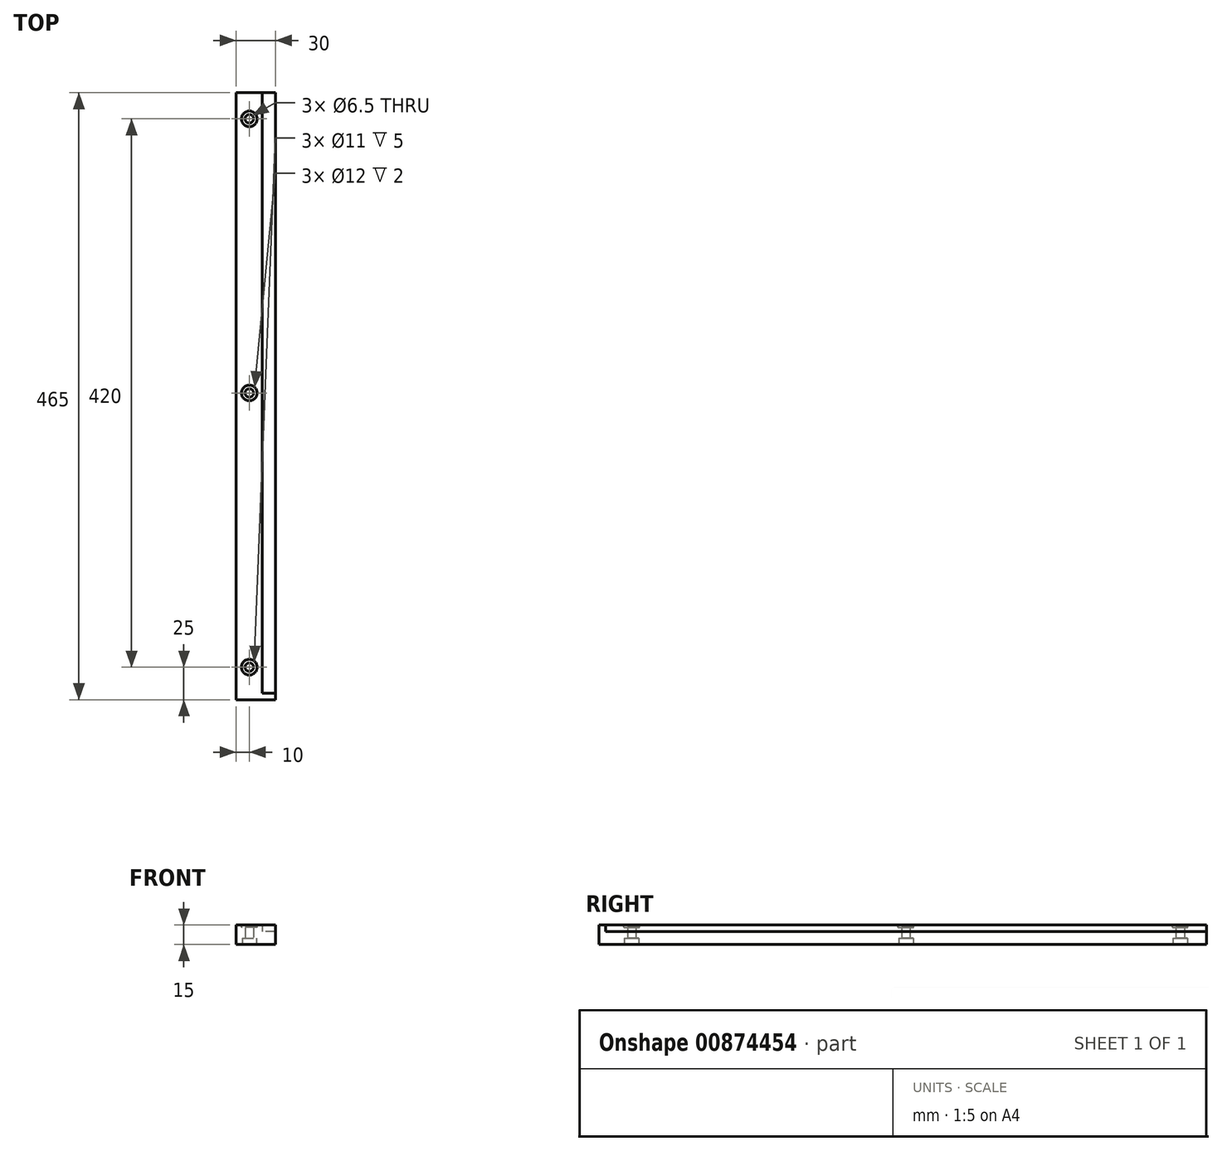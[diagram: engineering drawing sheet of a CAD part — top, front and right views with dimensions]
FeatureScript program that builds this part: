
annotation { "Feature Type Name" : "Feature", "Feature Type Description" : "" }
export const myFeature = defineFeature(function(context is Context, id is Id, definition is map)
    precondition{}
    {
        {
            var Q0;
            Q0=qCreatedBy(makeId("Front.planeOp"),FACE);
            var sketch = newSketch(context, id + "F0", { "sketchPlane" : qUnion([Q0])});
            skLineSegment(sketch, "E0.bottom", {"start": v(0, 0) * mm, "end": v(30, 0) * mm});
            skLineSegment(sketch, "E0.top", {"start": v(0, 15) * mm, "end": v(20, 15) * mm});
            skLineSegment(sketch, "E0.left", {"start": v(0, 0) * mm, "end": v(0, 15) * mm});
            skLineSegment(sketch, "E0.right", {"start": v(30, 0) * mm, "end": v(30, 10) * mm});
            skLineSegment(sketch, "E1.top", {"start": v(30, 10) * mm, "end": v(20, 10) * mm});
            skLineSegment(sketch, "E1.right", {"start": v(20, 15) * mm, "end": v(20, 10) * mm});
            skSolve(sketch);
        }
        {
            var Q0;
            Q0=makeQuery(id+"F0.imprint","IMPRINT",FACE,{"disambiguationData":[TD([[makeQuery(id+"F0.imprint","IMPRINT",EDGE,{"derivedFrom":sQuery(id+"F0.wireOp",EDGE,"E0.bottom")}),1.0]])]});
            extrude(context, id + "F1", {"entities" : qUnion([Q0]), "oppositeDirection" : true, "depth" : 460 * mm, "offsetDistance" : 25 * mm});
        }
        {
            var Q0;
            Q0=makeQuery(id+"F1.opExtrude","SWEPT_FACE",FACE,{"disambiguationData":[OSD([sQuery(id+"F0.wireOp",EDGE,"E0.bottom")])]});
            var sketch = newSketch(context, id + "F2", { "sketchPlane" : qUnion([Q0])});
            skCircle(sketch, "E2", {"center": v(10, -20) * mm, "radius": 2.5 * mm});
            skCircle(sketch, "E3", {"center": v(10, -230) * mm, "radius": 2.5 * mm});
            skCircle(sketch, "E4", {"center": v(10, -440) * mm, "radius": 2.5 * mm});
            skSolve(sketch);
        }
        {
            var Q0;
            Q0=sQuery(id+"F2.wireOp",VERTEX,"E4.center");
            var Q1;
            Q1=sQuery(id+"F2.wireOp",VERTEX,"E3.center");
            var Q2;
            Q2=sQuery(id+"F2.wireOp",VERTEX,"E2.center");
            var Q3;
            Q3=makeQuery(id+"F1.opExtrude","SWEPT_BODY",BODY,{"disambiguationData":[OSD([sQuery(id+"F0.wireOp",EDGE,"E0.bottom"),sQuery(id+"F0.wireOp",EDGE,"E0.top"),sQuery(id+"F0.wireOp",EDGE,"E0.left"),sQuery(id+"F0.wireOp",EDGE,"E0.right"),sQuery(id+"F0.wireOp",EDGE,"E1.top"),sQuery(id+"F0.wireOp",EDGE,"E1.right")])]});
            hole(context, id + "F3", {"style" : HoleStyle.C_BORE, "endStyle" : HoleEndStyle.BLIND, "holeDiameter" : 6.5 * mm, "cBoreDiameter" : 11 * mm, "cBoreDepth" : 5 * mm, "majorDiameter" : 5 * mm, "holeDepth" : 15 * mm, "isTappedThrough" : true, "tappedDepth" : 12 * mm, "tapClearance" : 3, "locations" : qUnion([Q0, Q1, Q2]), "scope" : qUnion([Q3])});
        }
        {
            var Q0;
            Q0=makeQuery(id+"F1.opExtrude","SWEPT_FACE",FACE,{"disambiguationData":[OSD([sQuery(id+"F0.wireOp",EDGE,"E0.top")])]});
            var sketch = newSketch(context, id + "F4", { "sketchPlane" : qUnion([Q0])});
            skCircle(sketch, "E5", {"center": v(10, 20) * mm, "radius": 5 * mm});
            skCircle(sketch, "E6", {"center": v(10, 230) * mm, "radius": 5 * mm});
            skCircle(sketch, "E7", {"center": v(10, 440) * mm, "radius": 5 * mm});
            skSolve(sketch);
        }
        {
            var Q0;
            Q0=sQuery(id+"F4.wireOp",VERTEX,"E7.center");
            var Q1;
            Q1=sQuery(id+"F4.wireOp",VERTEX,"E6.center");
            var Q2;
            Q2=sQuery(id+"F4.wireOp",VERTEX,"E5.center");
            var Q3;
            Q3=makeQuery(id+"F1.opExtrude","SWEPT_BODY",BODY,{"disambiguationData":[OSD([sQuery(id+"F0.wireOp",EDGE,"E0.bottom"),sQuery(id+"F0.wireOp",EDGE,"E0.top"),sQuery(id+"F0.wireOp",EDGE,"E0.left"),sQuery(id+"F0.wireOp",EDGE,"E0.right"),sQuery(id+"F0.wireOp",EDGE,"E1.top"),sQuery(id+"F0.wireOp",EDGE,"E1.right")])]});
            hole(context, id + "F5", {"style" : HoleStyle.C_BORE, "endStyle" : HoleEndStyle.BLIND, "holeDiameter" : 6.5 * mm, "cBoreDiameter" : 12 * mm, "cBoreDepth" : 2 * mm, "majorDiameter" : 5 * mm, "holeDepth" : 15 * mm, "isTappedThrough" : true, "tappedDepth" : 12 * mm, "tapClearance" : 3, "locations" : qUnion([Q0, Q1, Q2]), "scope" : qUnion([Q3])});
        }
        {
            var Q0;
            Q0=makeQuery(id+"F1.opExtrude","CAP_FACE",FACE,{"disambiguationData":[OSD([sQuery(id+"F0.wireOp",EDGE,"E0.bottom"),sQuery(id+"F0.wireOp",EDGE,"E0.top"),sQuery(id+"F0.wireOp",EDGE,"E0.left"),sQuery(id+"F0.wireOp",EDGE,"E0.right"),sQuery(id+"F0.wireOp",EDGE,"E1.top"),sQuery(id+"F0.wireOp",EDGE,"E1.right")])],"isStart":true});
            var sketch = newSketch(context, id + "F6", { "sketchPlane" : qUnion([Q0])});
            skLineSegment(sketch, "E8.bottom", {"start": v(0, 0) * mm, "end": v(30, 0) * mm});
            skLineSegment(sketch, "E8.top", {"start": v(0, 15) * mm, "end": v(30, 15) * mm});
            skLineSegment(sketch, "E8.left", {"start": v(0, 0) * mm, "end": v(0, 15) * mm});
            skLineSegment(sketch, "E8.right", {"start": v(30, 0) * mm, "end": v(30, 15) * mm});
            skSolve(sketch);
        }
        {
            var Q0;
            Q0 = qSketchRegion(id + "F6", true);
            extrude(context, id + "F7", {"entities" : qUnion([Q0]), "operationType" : NewBodyOperationType.ADD, "depth" : 5 * mm, "offsetDistance" : 25 * mm});
        }
    });
